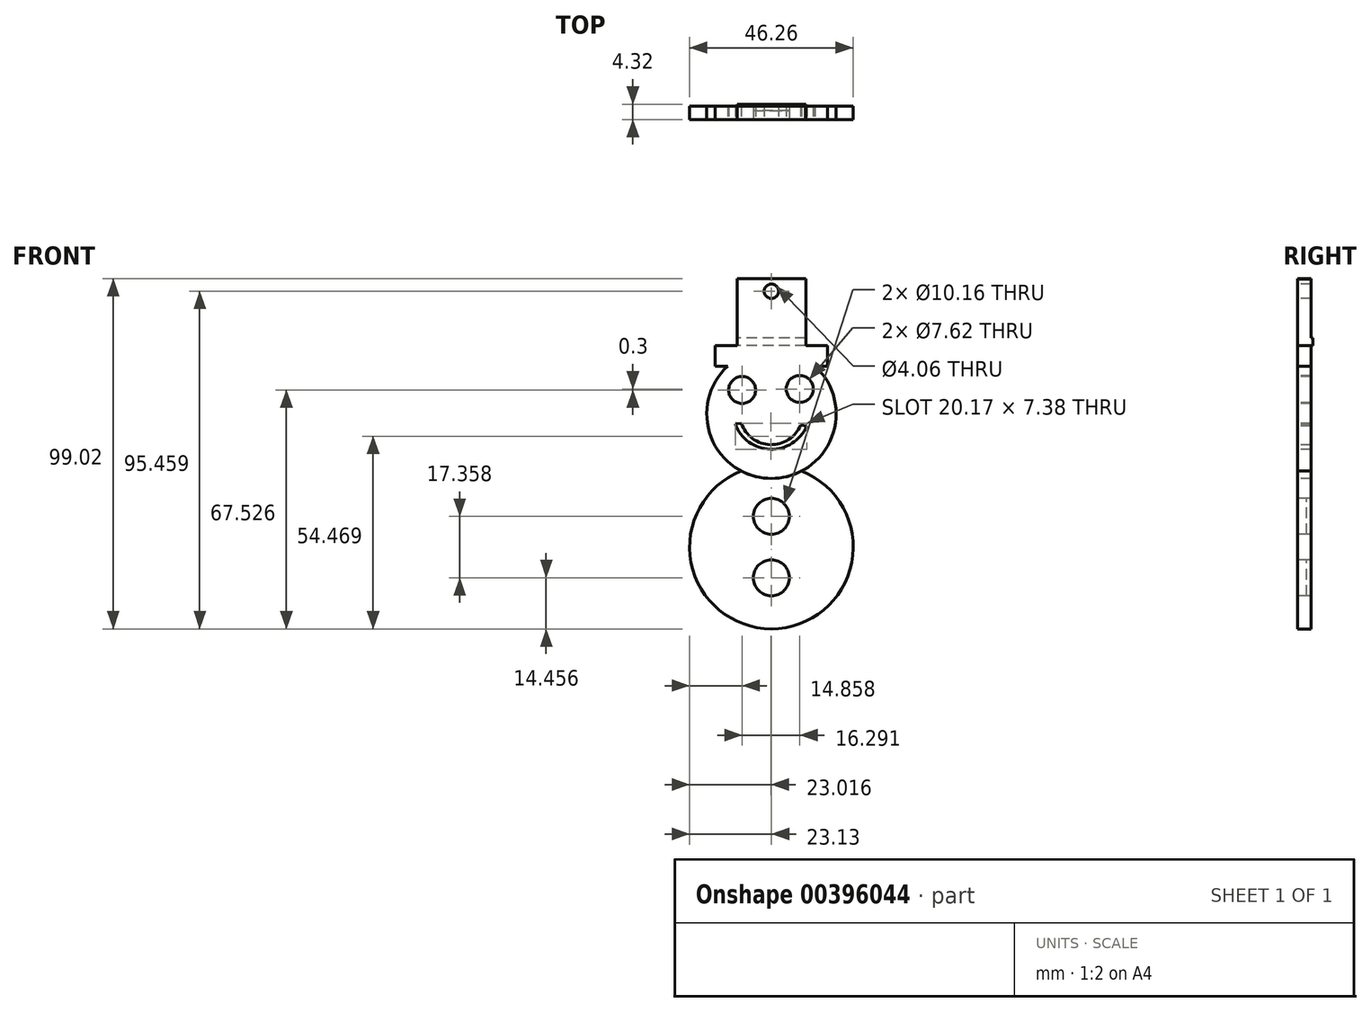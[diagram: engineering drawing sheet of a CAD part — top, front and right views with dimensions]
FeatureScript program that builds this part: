
annotation { "Feature Type Name" : "Feature", "Feature Type Description" : "" }
export const myFeature = defineFeature(function(context is Context, id is Id, definition is map)
    precondition{}
    {
        {
            var Q0;
            Q0=qCreatedBy(makeId("Front.planeOp"),FACE);
            var sketch = newSketch(context, id + "F0", { "sketchPlane" : qUnion([Q0])});
            skCircle(sketch, "E0", {"center": v(0, -37.67) * mm, "radius": 23.13 * mm});
            skArc(sketch, "E1", {"start": v(-12.32, 13.5) * mm, "mid": v(0, -18.28) * mm, "end": v(12.32, 13.5) * mm});
            skLineSegment(sketch, "E2.top", {"start": v(-15.85, 13.5) * mm, "end": v(15.85, 13.5) * mm});
            skLineSegment(sketch, "E2.left", {"start": v(-15.85, 19.24) * mm, "end": v(-15.85, 13.5) * mm});
            skLineSegment(sketch, "E2.right", {"start": v(15.85, 19.24) * mm, "end": v(15.85, 13.5) * mm});
            skLineSegment(sketch, "E3.top", {"start": v(-9.65, 38.22) * mm, "end": v(9.65, 38.22) * mm});
            skLineSegment(sketch, "E3.left", {"start": v(-9.65, 19.24) * mm, "end": v(-9.65, 38.22) * mm});
            skLineSegment(sketch, "E3.right", {"start": v(9.65, 19.24) * mm, "end": v(9.65, 38.22) * mm});
            skCircle(sketch, "E4", {"center": v(-8.27, 6.73) * mm, "radius": 3.81 * mm});
            skCircle(sketch, "E5", {"center": v(8.02, 7.03) * mm, "radius": 3.81 * mm});
            skArc(sketch, "E6", {"start": v(-10.2, -2.86) * mm, "mid": v(-0.31, -10.02) * mm, "end": v(9.97, -3.45) * mm});
            skArc(sketch, "E7", {"start": v(-8.49, -2.64) * mm, "mid": v(-0.3, -8.72) * mm, "end": v(8.28, -3.2) * mm});
            skLineSegment(sketch, "E8", {"start": v(-8.49, -2.64) * mm, "end": v(-10.2, -2.86) * mm});
            skLineSegment(sketch, "E9", {"start": v(8.28, -3.2) * mm, "end": v(9.97, -3.45) * mm});
            skCircle(sketch, "E10", {"center": v(0, -28.99) * mm, "radius": 5.08 * mm});
            skCircle(sketch, "E11", {"center": v(0, -46.34) * mm, "radius": 5.08 * mm});
            skCircle(sketch, "E12", {"center": v(0, 34.66) * mm, "radius": 2.03 * mm});
            skLineSegment(sketch, "E13.trimOffspring", {"start": v(9.65, 19.24) * mm, "end": v(15.85, 19.24) * mm});
            skLineSegment(sketch, "E14", {"start": v(-9.65, 19.24) * mm, "end": v(-15.85, 19.24) * mm});
            skSolve(sketch);
        }
        {
            var Q0;
            Q0=makeQuery(id+"F0.imprint","IMPRINT",FACE,{"disambiguationData":[TD([[makeQuery(id+"F0.imprint","IMPRINT",EDGE,{"derivedFrom":sQuery(id+"F0.wireOp",EDGE,"E3.bottom")}),1.0]])]});
            var Q1;
            {var subQ14=sQuery(id+"F0.wireOp",EDGE,"E2.left");Q1=makeQuery(id+"F0.imprint","IMPRINT",FACE,{"disambiguationData":[TD([[makeQuery(id+"F0.imprint","IMPRINT",EDGE,{"derivedFrom":subQ14}),1.0]])]});}
            var Q2;
            Q2=makeQuery(id+"F0.imprint","IMPRINT",FACE,{"disambiguationData":[TD([[makeQuery(id+"F0.imprint","IMPRINT",EDGE,{"derivedFrom":sQuery(id+"F0.wireOp",EDGE,"E4")}),-1.0]])]});
            var Q3;
            {var subQ0=sQuery(id+"F0.wireOp",EDGE,"E1");var subQ1=sQuery(id+"F0.wireOp",EDGE,"E0");var subQ2=makeQuery(id+"F0.imprint","INTERSECT",VERTEX,{"disambiguationData":[OD(0.0)],"derivedFrom":[subQ1,subQ0]});Q3=makeQuery(id+"F0.imprint","IMPRINT",FACE,{"disambiguationData":[TD([[makeQuery(id+"F0.imprint","IMPRINT",EDGE,{"disambiguationData":[TD([[subQ2,-1.0]])],"derivedFrom":subQ1}),1.0]])]});}
            var Q4;
            Q4=makeQuery(id+"F0.imprint","IMPRINT",FACE,{"disambiguationData":[TD([[makeQuery(id+"F0.imprint","IMPRINT",EDGE,{"derivedFrom":sQuery(id+"F0.wireOp",EDGE,"d47015dd-9014-4c70-bc6b-3e0848645b5b.sketch_text.stroke-0")}),1.0]])]});
            var Q5;
            Q5=makeQuery(id+"F0.imprint","IMPRINT",FACE,{"disambiguationData":[TD([[makeQuery(id+"F0.imprint","IMPRINT",EDGE,{"derivedFrom":sQuery(id+"F0.wireOp",EDGE,"d47015dd-9014-4c70-bc6b-3e0848645b5b.sketch_text.stroke-105")}),1.0]])]});
            var Q6;
            {var subQ0=sQuery(id+"F0.wireOp",EDGE,"d47015dd-9014-4c70-bc6b-3e0848645b5b.sketch_text.stroke-139");Q6=makeQuery(id+"F0.imprint","IMPRINT",FACE,{"disambiguationData":[TD([[makeQuery(id+"F0.imprint","IMPRINT",EDGE,{"derivedFrom":subQ0}),1.0]])]});}
            var Q7;
            {var subQ0=sQuery(id+"F0.wireOp",EDGE,"d47015dd-9014-4c70-bc6b-3e0848645b5b.sketch_text.stroke-5");Q7=makeQuery(id+"F0.imprint","IMPRINT",FACE,{"disambiguationData":[TD([[makeQuery(id+"F0.imprint","IMPRINT",EDGE,{"derivedFrom":subQ0}),1.0]])]});}
            var Q8;
            {var subQ5=sQuery(id+"F0.wireOp",EDGE,"d47015dd-9014-4c70-bc6b-3e0848645b5b.sketch_text.stroke-137");Q8=makeQuery(id+"F0.imprint","IMPRINT",FACE,{"disambiguationData":[TD([[makeQuery(id+"F0.imprint","IMPRINT",EDGE,{"derivedFrom":subQ5}),1.0]])]});}
            extrude(context, id + "F1", {"entities" : qUnion([Q0, Q1, Q2, Q3, Q4, Q5, Q6, Q7, Q8]), "oppositeDirection" : true, "depth" : 3.8 * mm});
        }
        {
            var Q0;
            {var subQ0=sQuery(id+"F0.wireOp",EDGE,"E1");var subQ1=sQuery(id+"F0.wireOp",EDGE,"E0");var subQ2=makeQuery(id+"F0.imprint","INTERSECT",VERTEX,{"disambiguationData":[OD(0.0)],"derivedFrom":[subQ1,subQ0]});Q0=makeQuery(id+"F0.imprint","IMPRINT",FACE,{"disambiguationData":[TD([[makeQuery(id+"F0.imprint","IMPRINT",EDGE,{"disambiguationData":[TD([[subQ2,1.0]])],"derivedFrom":subQ1}),1.0]])]});}
            extrude(context, id + "F2", {"entities" : qUnion([Q0]), "oppositeDirection" : true, "depth" : 3.8 * mm});
        }
        {
            var Q0;
            Q0=qCreatedBy(makeId("Front.planeOp"),FACE);
            var sketch = newSketch(context, id + "F3", { "sketchPlane" : qUnion([Q0])});
            skCircle(sketch, "E15", {"center": v(0, -37.76) * mm, "radius": 23.13 * mm});
            skCircle(sketch, "E16", {"center": v(0, -0.08) * mm, "radius": 18.28 * mm});
            skLineSegment(sketch, "E17.bottom", {"start": v(-15.85, 19.16) * mm, "end": v(15.85, 19.16) * mm});
            skLineSegment(sketch, "E17.left", {"start": v(-15.85, 19.16) * mm, "end": v(-15.85, 13.42) * mm});
            skLineSegment(sketch, "E17.right", {"start": v(15.85, 19.16) * mm, "end": v(15.85, 13.42) * mm});
            skLineSegment(sketch, "E18.top", {"start": v(-9.12, 38.14) * mm, "end": v(9.77, 38.14) * mm});
            skLineSegment(sketch, "E18.left", {"start": v(-9.12, 19.16) * mm, "end": v(-9.12, 38.14) * mm});
            skLineSegment(sketch, "E18.right", {"start": v(9.77, 19.16) * mm, "end": v(9.77, 38.14) * mm});
            skSolve(sketch);
        }
        {
            var Q0;
            Q0=makeQuery(id+"F0.imprint","IMPRINT",FACE,{"disambiguationData":[TD([[makeQuery(id+"F0.imprint","IMPRINT",EDGE,{"derivedFrom":sQuery(id+"F0.wireOp",EDGE,"E11")}),1.0]])]});
            var Q1;
            Q1=makeQuery(id+"F0.imprint","IMPRINT",FACE,{"disambiguationData":[TD([[makeQuery(id+"F0.imprint","IMPRINT",EDGE,{"derivedFrom":sQuery(id+"F0.wireOp",EDGE,"E10")}),1.0]])]});
            extrude(context, id + "F4", {"entities" : qUnion([Q0, Q1]), "oppositeDirection" : true, "depth" : 2.54 * mm});
        }
        {
            var Q0;
            Q0=makeQuery(id+"F3.imprint","IMPRINT",FACE,{"disambiguationData":[TD([[makeQuery(id+"F3.imprint","IMPRINT",EDGE,{"derivedFrom":sQuery(id+"F3.wireOp",EDGE,"E18.top")}),-1.0]])]});
            extrude(context, id + "F5", {"entities" : qUnion([Q0]), "operationType" : NewBodyOperationType.ADD, "oppositeDirection" : true, "depth" : 3.8 * mm});
        }
        {
            var Q0;
            Q0=makeQuery(id+"F5.boolean.opBoolean","MERGE",FACE,{"derivedFrom":[makeQuery(id+"F1.opExtrude","CAP_FACE",FACE,{"disambiguationData":[OSD([sQuery(id+"F0.wireOp",EDGE,"E1"),sQuery(id+"F0.wireOp",EDGE,"E2.top"),sQuery(id+"F0.wireOp",EDGE,"E2.left"),sQuery(id+"F0.wireOp",EDGE,"E2.right"),sQuery(id+"F0.wireOp",EDGE,"E3.top"),sQuery(id+"F0.wireOp",EDGE,"E3.left"),sQuery(id+"F0.wireOp",EDGE,"E3.right"),sQuery(id+"F0.wireOp",EDGE,"E12"),sQuery(id+"F0.wireOp",EDGE,"E13.trimOffspring"),sQuery(id+"F0.wireOp",EDGE,"E14")])],"isStart":false}),makeQuery(id+"F5.opExtrude","CAP_FACE",FACE,{"disambiguationData":[OSD([sQuery(id+"F3.wireOp",EDGE,"E17.bottom"),sQuery(id+"F3.wireOp",EDGE,"E18.top"),sQuery(id+"F3.wireOp",EDGE,"E18.left"),sQuery(id+"F3.wireOp",EDGE,"E18.right")])],"isStart":false})]});
            var sketch = newSketch(context, id + "F6", { "sketchPlane" : qUnion([Q0])});
            skLineSegment(sketch, "E19.bottom", {"start": v(-9.77, 19.24) * mm, "end": v(9.65, 19.24) * mm});
            skLineSegment(sketch, "E19.top", {"start": v(-9.77, 21.38) * mm, "end": v(9.65, 21.38) * mm});
            skLineSegment(sketch, "E19.left", {"start": v(-9.77, 19.24) * mm, "end": v(-9.77, 21.38) * mm});
            skLineSegment(sketch, "E19.right", {"start": v(9.65, 19.24) * mm, "end": v(9.65, 21.38) * mm});
            skSolve(sketch);
        }
        {
            var Q0;
            Q0=makeQuery(id+"F6.imprint","IMPRINT",FACE,{"disambiguationData":[TD([[makeQuery(id+"F6.imprint","IMPRINT",EDGE,{"derivedFrom":sQuery(id+"F6.wireOp",EDGE,"E19.bottom")}),1.0]])]});
            extrude(context, id + "F7", {"entities" : qUnion([Q0]), "operationType" : NewBodyOperationType.ADD, "depth" : 0.5 * mm});
        }
        {
            var Q0;
            Q0=makeQuery(id+"F0.imprint","IMPRINT",FACE,{"disambiguationData":[TD([[makeQuery(id+"F0.imprint","IMPRINT",EDGE,{"derivedFrom":sQuery(id+"F0.wireOp",EDGE,"E12")}),1.0]])]});
            extrude(context, id + "F8", {"entities" : qUnion([Q0]), "operationType" : NewBodyOperationType.REMOVE, "oppositeDirection" : true, "depth" : 25.4 * mm});
        }
    });
